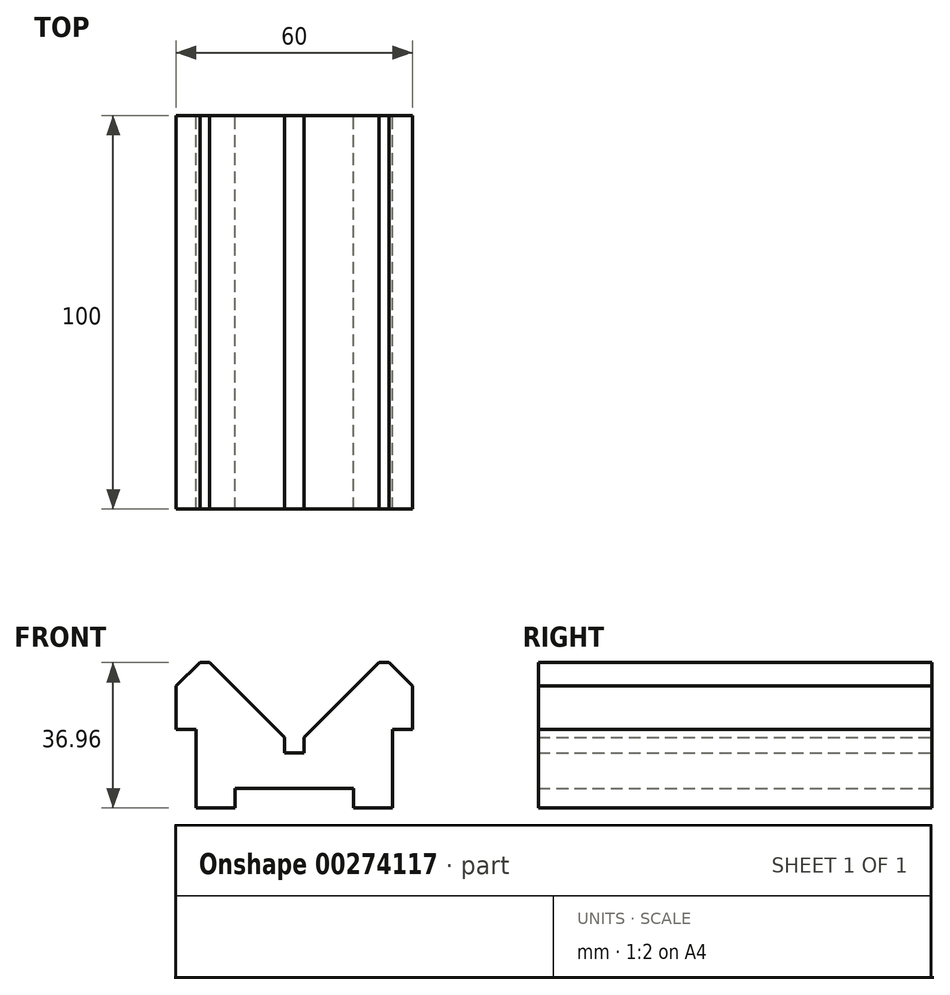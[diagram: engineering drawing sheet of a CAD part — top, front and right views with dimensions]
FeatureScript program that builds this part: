
annotation { "Feature Type Name" : "Feature", "Feature Type Description" : "" }
export const myFeature = defineFeature(function(context is Context, id is Id, definition is map)
    precondition{}
    {
        {
            var Q0;
            Q0=qCreatedBy(makeId("Front.planeOp"),FACE);
            var sketch = newSketch(context, id + "F0", { "sketchPlane" : qUnion([Q0])});
            skLineSegment(sketch, "E0.bottom", {"start": v(-24, 31.96) * mm, "end": v(-21.5, 31.96) * mm});
            skLineSegment(sketch, "E0.top", {"start": v(-25, -5) * mm, "end": v(-15, -5) * mm});
            skLineSegment(sketch, "E0.left", {"start": v(-30, 25.96) * mm, "end": v(-30, 15) * mm});
            skLineSegment(sketch, "E0.right", {"start": v(30, 25.96) * mm, "end": v(30, 15) * mm});
            skLineSegment(sketch, "E1", {"start": v(-15, 0) * mm, "end": v(15, 0) * mm});
            skLineSegment(sketch, "E2", {"start": v(-15, -5) * mm, "end": v(-15, 0) * mm});
            skLineSegment(sketch, "E3", {"start": v(15, -5) * mm, "end": v(15, 0) * mm});
            skLineSegment(sketch, "E4", {"start": v(-30, 15) * mm, "end": v(-25, 15) * mm});
            skPoint(sketch, "E5.trimOffspring.start.orphan", {"position": v(-30, 0) * mm});
            skPoint(sketch, "E6.orphan", {"position": v(-30, -5) * mm});
            skLineSegment(sketch, "E7.trimOffspring", {"start": v(15, -5) * mm, "end": v(25, -5) * mm});
            skLineSegment(sketch, "E8.trimOffspring", {"start": v(-25, 15) * mm, "end": v(-25, -5) * mm});
            skLineSegment(sketch, "E9.trimOffspring", {"start": v(25, 15) * mm, "end": v(25, -5) * mm});
            skPoint(sketch, "E10.end.orphan", {"position": v(-24, 25.96) * mm});
            skPoint(sketch, "E11.start.orphan", {"position": v(25.75, 25.96) * mm});
            skPoint(sketch, "E12.orphan", {"position": v(30, 25.96) * mm});
            skLineSegment(sketch, "E13", {"start": v(-30, 25.96) * mm, "end": v(-24, 31.96) * mm});
            skLineSegment(sketch, "E14", {"start": v(30, 25.96) * mm, "end": v(24, 31.96) * mm});
            skLineSegment(sketch, "E15", {"start": v(-2.5, 8.96) * mm, "end": v(2.5, 8.96) * mm});
            skLineSegment(sketch, "E16.trimOffspring", {"start": v(25, 15) * mm, "end": v(30, 15) * mm});
            skPoint(sketch, "E17.end.orphan", {"position": v(2.5, 31.96) * mm});
            skLineSegment(sketch, "E18.trimOffspring", {"start": v(21.5, 31.96) * mm, "end": v(24, 31.96) * mm});
            skLineSegment(sketch, "E19", {"start": v(2.5, 12.96) * mm, "end": v(2.5, 8.96) * mm});
            skLineSegment(sketch, "E20", {"start": v(-2.5, 12.96) * mm, "end": v(-2.5, 8.96) * mm});
            skLineSegment(sketch, "E21", {"start": v(21.5, 31.96) * mm, "end": v(2.5, 12.96) * mm});
            skLineSegment(sketch, "E22", {"start": v(-21.5, 31.96) * mm, "end": v(-2.5, 12.96) * mm});
            skPoint(sketch, "E23.end.orphan", {"position": v(-21.5, 25.96) * mm});
            skPoint(sketch, "E24.trimOffspring.start.orphan", {"position": v(21.5, 25.96) * mm});
            skSolve(sketch);
        }
        {
            var Q0;
            Q0 = qSketchRegion(id + "F0", true);
            extrude(context, id + "F1", {"entities" : qUnion([Q0]), "depth" : 100 * mm});
        }
    });
